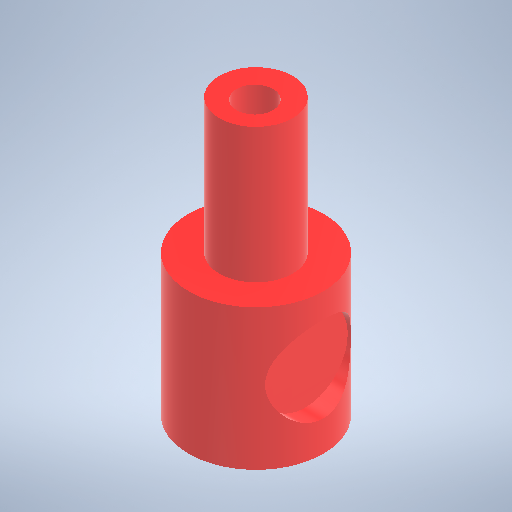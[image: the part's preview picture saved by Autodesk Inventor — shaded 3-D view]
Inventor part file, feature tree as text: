
AUTODESK INVENTOR PART (.ipt)
format: ipt  version: 2025 (Build 290162010, 162A)  size: 263,680 bytes
history: native  units: mm
features: sketch x4, hole x3, revolve x1, plane x1
ambient origin geometry x8: Origin, YZ Plane, XZ Plane, XY Plane, X Axis, Y Axis, Z Axis, Center Point
bodies: Solid1 (feature_tree)
feature tree (9):
  revolve  "Revolution1"  [1 undecoded]
  hole  "Hole1"  [1 undecoded]
  hole  "Hole2"  [1 undecoded]
  plane  "Work Plane1"
  hole  "Hole3"  [1 undecoded]
  sketch  "Sketch1"  dims[d0=11.0mm d1=6.0mm]
  sketch  "Sketch2"  dims[d2=11.0mm d3=11.5mm]
  sketch  "Sketch3"  dims[d4=90.0deg]
  sketch  "Sketch4"  dims[d5=6.0mm d6=6.0mm d7=9.0mm d8=2.5mm d9=90.0deg d10=7.0mm d11=0.0mm d12=3.0mm d13=6.0mm d14=4.0mm d15=2.0mm d16=90.0deg d17=15.5mm d18=0.0mm d19=5.5mm d20=6.0mm d21=7.0mm d22=6.0mm d23=4.0mm d24=2.0mm d25=90.0deg d26=1.5mm d27=0.0mm]
note: 4 required parameter values undecoded (feature->parameter linkage not recoverable at this tier; creation-order binding heuristic only, values carry confidence <= 0.55)